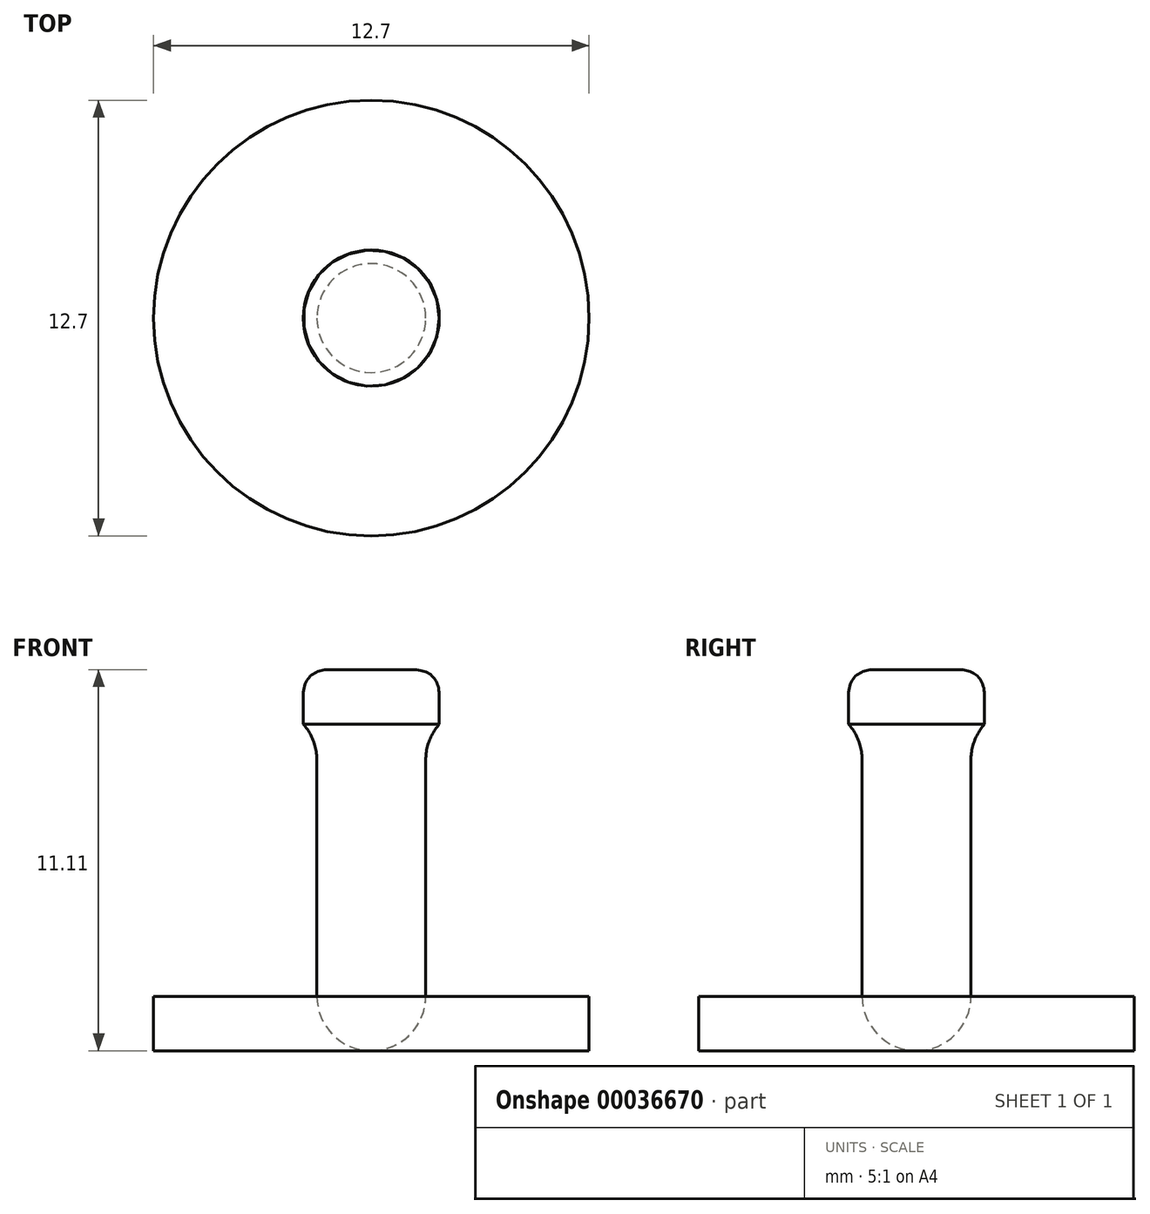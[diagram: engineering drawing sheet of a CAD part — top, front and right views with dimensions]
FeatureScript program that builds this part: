
annotation { "Feature Type Name" : "Feature", "Feature Type Description" : "" }
export const myFeature = defineFeature(function(context is Context, id is Id, definition is map)
    precondition{}
    {
        {
            var Q0;
            Q0=qCreatedBy(makeId("Top.planeOp"),FACE);
            var sketch = newSketch(context, id + "F0", { "sketchPlane" : qUnion([Q0])});
            skCircle(sketch, "E0", {"center": v(0, 0) * mm, "radius": 6.35 * mm});
            skCircle(sketch, "E1", {"center": v(0, 0) * mm, "radius": 1.59 * mm});
            skSolve(sketch);
        }
        {
            var Q0;
            Q0=makeQuery(id+"F0.imprint","IMPRINT",FACE,{"disambiguationData":[TD([[makeQuery(id+"F0.imprint","IMPRINT",EDGE,{"derivedFrom":sQuery(id+"F0.wireOp",EDGE,"E0")}),1.0]])]});
            var Q1;
            Q1=makeQuery(id+"F0.imprint","IMPRINT",FACE,{"disambiguationData":[TD([[makeQuery(id+"F0.imprint","IMPRINT",EDGE,{"derivedFrom":sQuery(id+"F0.wireOp",EDGE,"E1")}),1.0]])]});
            var Q2;
            Q2=makeQuery(id+"F0.imprint","IMPRINT",FACE,{"disambiguationData":[TD([[makeQuery(id+"F0.imprint","IMPRINT",EDGE,{"derivedFrom":sQuery(id+"F0.wireOp",EDGE,"E1")}),-1.0]])]});
            extrude(context, id + "F1", {"entities" : qUnion([Q0, Q1, Q2]), "depth" : 1.59 * mm});
        }
        {
            var Q0;
            Q0=makeQuery(id+"F0.imprint","IMPRINT",FACE,{"disambiguationData":[TD([[makeQuery(id+"F0.imprint","IMPRINT",EDGE,{"derivedFrom":sQuery(id+"F0.wireOp",EDGE,"E1")}),1.0]])]});
            var Q1;
            Q1=sQuery(id+"F0.wireOp",EDGE,"E1");
            extrude(context, id + "F2", {"entities" : qUnion([Q0]), "surfaceEntities" : qUnion([Q1]), "depth" : 9.52 * mm});
        }
        {
            var Q0;
            Q0=makeQuery(id+"F2.opExtrude","CAP_FACE",FACE,{"disambiguationData":[OSD([sQuery(id+"F0.wireOp",EDGE,"E1")])],"isStart":false});
            var sketch = newSketch(context, id + "F3", { "sketchPlane" : qUnion([Q0])});
            skCircle(sketch, "E2", {"center": v(0, 0) * mm, "radius": 1.98 * mm});
            skSolve(sketch);
        }
        {
            var Q0;
            Q0 = qSketchRegion(id + "F3", true);
            extrude(context, id + "F4", {"entities" : qUnion([Q0]), "operationType" : NewBodyOperationType.ADD, "depth" : 1.59 * mm});
        }
        {
            var Q0;
            Q0=makeQuery(id+"F4.opExtrude","CAP_EDGE",EDGE,{"disambiguationData":[OSD([sQuery(id+"F3.wireOp",EDGE,"E2")])],"isStart":false});
            fillet(context, id + "F5", {"entities" : qUnion([Q0]), "radius" : 0.8 * mm, "rho" : 0.5, "crossSection" : FilletCrossSection.CONIC, "allowEdgeOverflow" : false});
        }
        {
            var Q0;
            Q0=makeQuery(id+"F2.opExtrude","SWEPT_FACE",FACE,{"disambiguationData":[OSD([sQuery(id+"F0.wireOp",EDGE,"E1")])]});
            fillet(context, id + "F6", {"entities" : qUnion([Q0]), "radius" : 1.59 * mm, "tangentPropagation" : true, "allowEdgeOverflow" : false});
        }
    });
